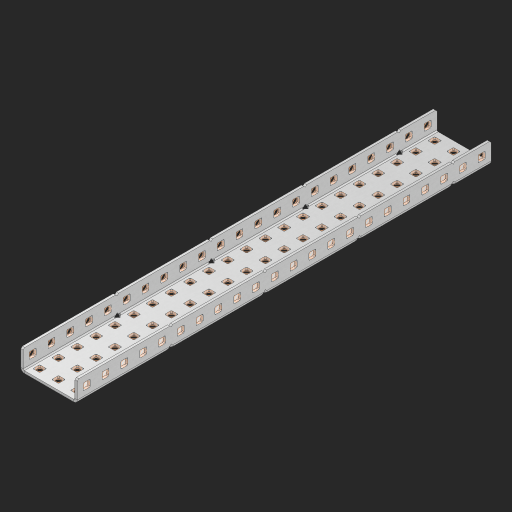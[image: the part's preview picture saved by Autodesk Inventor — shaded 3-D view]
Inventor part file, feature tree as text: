
AUTODESK INVENTOR PART (.ipt)
format: ipt  version: 2023 (Build 270158000, 158)  size: 1,453,568 bytes
history: native  units: in
note: dims shown in document units (in); Inventor stores cm internally (conversion verified against a paired STEP export)
features: other x115, extrude x109, sheet_metal_op x10, sketch x8, mirror x1, pattern_linear x1, chamfer x1
ambient origin geometry x8: Origin, YZ Plane, XZ Plane, XY Plane, X Axis, Y Axis, Z Axis, Center Point
bodies: Solid1 (feature_tree), Body (feature_tree)
feature tree (245):
  other  "Flange Pattern Plane"
  sheet_metal_op  "Flange Pattern"
  sheet_metal_op  "Body Pattern"
  other  "Arc Length"
  mirror  "Notch Mirror"
  pattern_linear  "Notch Pattern"  Spacing1=0.25in  [1 undecoded]
  chamfer  "End Chamfer"
  extrude  "Half Cut"  Depth=0.0625in
  sketch  "Sketch1"  dims[d0=1.5in]
  other  "Plate1"
  sketch  "Sketch2"  dims[d1=11.0in]
  other  "Plate2"
  sheet_metal_op  "Bend1"
  sheet_metal_op  "Corner1"
  sketch  "Sketch3"  dims[d2=0.0625in]
  other  "Flange Pattern Sketch"
  sketch  "Sketch7"  dims[d3=0.0625in]
  other  "Srf1"
  other  "Srf2"
  sketch  "Sketch8"  dims[d4=0.0312in]
  sketch  "Sketch9"  dims[d5=0.125in]
  other  "Srf91"
  sheet_metal_op  "Body Pattern Sketch"
  other  "Srf92"
  sketch  "Sketch13"  dims[d6=0.0625in]
  sketch  "Sketch14"  dims[d7=0.5in d8=90.0deg d9=0.0312in d10=0.25in d11=0.0625in d12=0.0625in d16=0.182in d17=0.02in d18=0.0625in d19=0.0in d20=0.25in d21=0.25in d46=0.172in d47=1.0in d48=0.0in d49=0.182in d50=0.02in d51=0.25in d52=0.25in d53=0.0625in d54=0.0in d55=0.172in d56=1.0in d57=0.0in d60=8.6614in d62=0.5in d63=1.1811in d65=0.5in d85=0.1473in d86=0.1782in d88=0.04in d89=0.0625in d90=0.0in d91=0.04in d92=0.0491in d95=2.5in d96=0.04in d97=0.25in d98=45.0deg d101=0.0in d102=2.497in d131=1.5in d132=8.6614in d134=0.5in d139=0.5in]
  other  "Srf856"
  other  "Srf1310"
  other  "Srf1311"
  other  "Srf1312"
  other  "Srf1376"
  other  "Srf1377"
  other  "Srf1728"
  other  "Srf1755"
  other  "Srf1878"
  other  "Srf1879"
  other  "Srf1880"
  other  "Srf1881"
  other  "Srf1882"
  other  "Srf1883"
  other  "Srf1884"
  other  "Srf1885"
  other  "Srf1886"
  other  "Srf1887"
  other  "Srf1888"
  other  "Srf1889"
  other  "Srf1890"
  other  "Srf1891"
  other  "Srf1892"
  other  "Srf1893"
  other  "Srf1894"
  other  "Srf1895"
  other  "Srf1896"
  other  "Srf1897"
  other  "Srf1898"
  other  "Srf1899"
  other  "Srf1900"
  other  "Srf1901"
  other  "Srf1902"
  other  "Srf1903"
  other  "Srf1904"
  other  "Srf1905"
  other  "Srf1906"
  other  "Srf1907"
  other  "Srf1908"
  other  "Srf1909"
  other  "Srf1910"
  other  "Srf1911"
  other  "Srf1912"
  other  "Srf1913"
  other  "Srf1914"
  other  "Srf1915"
  other  "Srf1942"
  other  "Srf1943"
  other  "Srf1944"
  other  "Srf1945"
  other  "Srf1946"
  other  "Srf1947"
  other  "Srf1948"
  other  "Srf1949"
  other  "Srf1950"
  other  "Srf1951"
  other  "Srf1952"
  other  "Srf1953"
  other  "Srf1954"
  other  "Srf1955"
  other  "Srf1956"
  other  "Srf1957"
  other  "Srf1958"
  other  "Srf1959"
  other  "Srf1960"
  other  "Srf1961"
  other  "Srf1962"
  other  "Srf1963"
  other  "Srf1964"
  other  "Srf1965"
  other  "Srf1966"
  other  "Srf1967"
  other  "Srf1968"
  other  "Srf1969"
  other  "Srf1970"
  other  "Srf1971"
  other  "Srf1972"
  other  "Srf1973"
  other  "Srf1974"
  other  "Srf1975"
  other  "Srf1976"
  other  "Srf1977"
  other  "Srf1978"
  other  "Srf1979"
  other  "Srf1980"
  other  "Srf1981"
  other  "Srf1982"
  other  "Srf1983"
  other  "Srf1984"
  other  "Srf1985"
  other  "Srf1986"
  other  "Srf1987"
  other  "Srf1988"
  other  "Srf1989"
  other  "Srf1990"
  other  "Srf1991"
  other  "Srf1992"
  other  "Srf1993"
  other  "Srf1994"
  other  "Srf1995"
  other  "Srf1996"
  other  "Srf1997"
  other  "Srf1998"
  other  "Srf1999"
  other  "Srf2000"
  other  "Srf2001"
  sheet_metal_op  "Flange Stamp"
  sheet_metal_op  "Flange Circle"
  sheet_metal_op  "Body Stamp"
  sheet_metal_op  "Body Circle"
  sheet_metal_op  "Notch"
  extrude  "ExtrusionSrf2"  Depth=0.0625in
  extrude  "ExtrusionSrf92"  Depth=1.5in
  extrude  "ExtrusionSrf856"  Depth=0.02in
  extrude  "ExtrusionSrf1310"  Depth=0.0625in
  extrude  "ExtrusionSrf1311"  TaperAngle=0.0deg  [1 undecoded]
  extrude  "ExtrusionSrf1312"  Depth=0.25in
  extrude  "ExtrusionSrf1376"  Depth=0.25in
  extrude  "ExtrusionSrf1377"  Depth=1.5in
  extrude  "ExtrusionSrf1728"  Depth=1.5in TaperAngle=0.0deg
  extrude  "ExtrusionSrf1755"  Depth=1.5in
  extrude  "ExtrusionSrf1878"  Depth=0.02in
  extrude  "ExtrusionSrf1879"  Depth=0.25in
  extrude  "ExtrusionSrf1880"  Depth=0.25in
  extrude  "ExtrusionSrf1881"  Depth=0.0625in
  extrude  "ExtrusionSrf1882"  TaperAngle=0.0deg  [1 undecoded]
  extrude  "ExtrusionSrf1883"  Depth=1.5in
  extrude  "ExtrusionSrf1884"  Depth=1.5in TaperAngle=0.0deg
  extrude  "ExtrusionSrf1885"  Depth=1.5in
  extrude  "ExtrusionSrf1886"  Depth=1.5in
  extrude  "ExtrusionSrf1887"  Depth=1.5in
  extrude  "ExtrusionSrf1888"  Depth=1.5in
  extrude  "ExtrusionSrf1889"  Depth=1.5in
  extrude  "ExtrusionSrf1890"  Depth=0.0625in
  extrude  "ExtrusionSrf1891"  TaperAngle=0.0deg  [1 undecoded]
  extrude  "ExtrusionSrf1892"  Depth=1.5in
  extrude  "ExtrusionSrf1893"  Depth=1.5in
  extrude  "ExtrusionSrf1894"  Depth=1.5in
  extrude  "ExtrusionSrf1895"  Depth=0.25in TaperAngle=45.0deg
  extrude  "ExtrusionSrf1896"  TaperAngle=0.0deg  [1 undecoded]
  extrude  "ExtrusionSrf1897"  Depth=1.5in
  extrude  "ExtrusionSrf1898"  Depth=1.5in
  extrude  "ExtrusionSrf1899"  Depth=1.5in
  extrude  "ExtrusionSrf1900"  Depth=1.5in
  extrude  "ExtrusionSrf1901"  Depth=1.5in
  extrude  "ExtrusionSrf1902"  [1 undecoded]
  extrude  "ExtrusionSrf1903"  [1 undecoded]
  extrude  "ExtrusionSrf1904"  [1 undecoded]
  extrude  "ExtrusionSrf1905"  [1 undecoded]
  extrude  "ExtrusionSrf1906"  [1 undecoded]
  extrude  "ExtrusionSrf1907"  [1 undecoded]
  extrude  "ExtrusionSrf1908"  [1 undecoded]
  extrude  "ExtrusionSrf1909"  [1 undecoded]
  extrude  "ExtrusionSrf1910"  [1 undecoded]
  extrude  "ExtrusionSrf1911"  [1 undecoded]
  extrude  "ExtrusionSrf1912"  [1 undecoded]
  extrude  "ExtrusionSrf1913"  [1 undecoded]
  extrude  "ExtrusionSrf1914"  [1 undecoded]
  extrude  "ExtrusionSrf1915"  [1 undecoded]
  extrude  "ExtrusionSrf1942"  [1 undecoded]
  extrude  "ExtrusionSrf1943"  [1 undecoded]
  extrude  "ExtrusionSrf1944"  [1 undecoded]
  extrude  "ExtrusionSrf1945"  [1 undecoded]
  extrude  "ExtrusionSrf1946"  [1 undecoded]
  extrude  "ExtrusionSrf1947"  [1 undecoded]
  extrude  "ExtrusionSrf1948"  [1 undecoded]
  extrude  "ExtrusionSrf1949"  [1 undecoded]
  extrude  "ExtrusionSrf1950"  [1 undecoded]
  extrude  "ExtrusionSrf1951"  [1 undecoded]
  extrude  "ExtrusionSrf1952"  [1 undecoded]
  extrude  "ExtrusionSrf1953"  [1 undecoded]
  extrude  "ExtrusionSrf1954"  [1 undecoded]
  extrude  "ExtrusionSrf1955"  [1 undecoded]
  extrude  "ExtrusionSrf1956"  [1 undecoded]
  extrude  "ExtrusionSrf1957"  [1 undecoded]
  extrude  "ExtrusionSrf1958"  [1 undecoded]
  extrude  "ExtrusionSrf1959"  [1 undecoded]
  extrude  "ExtrusionSrf1960"  [1 undecoded]
  extrude  "ExtrusionSrf1961"  [1 undecoded]
  extrude  "ExtrusionSrf1962"  [1 undecoded]
  extrude  "ExtrusionSrf1963"  [1 undecoded]
  extrude  "ExtrusionSrf1964"  [1 undecoded]
  extrude  "ExtrusionSrf1965"  [1 undecoded]
  extrude  "ExtrusionSrf1966"  [1 undecoded]
  extrude  "ExtrusionSrf1967"  [1 undecoded]
  extrude  "ExtrusionSrf1968"  [1 undecoded]
  extrude  "ExtrusionSrf1969"  [1 undecoded]
  extrude  "ExtrusionSrf1970"  [1 undecoded]
  extrude  "ExtrusionSrf1971"  [1 undecoded]
  extrude  "ExtrusionSrf1972"  [1 undecoded]
  extrude  "ExtrusionSrf1973"  [1 undecoded]
  extrude  "ExtrusionSrf1974"  [1 undecoded]
  extrude  "ExtrusionSrf1975"  [1 undecoded]
  extrude  "ExtrusionSrf1976"  [1 undecoded]
  extrude  "ExtrusionSrf1977"  [1 undecoded]
  extrude  "ExtrusionSrf1978"  [1 undecoded]
  extrude  "ExtrusionSrf1979"  [1 undecoded]
  extrude  "ExtrusionSrf1980"  [1 undecoded]
  extrude  "ExtrusionSrf1981"  [1 undecoded]
  extrude  "ExtrusionSrf1982"  [1 undecoded]
  extrude  "ExtrusionSrf1983"  [1 undecoded]
  extrude  "ExtrusionSrf1984"  [1 undecoded]
  extrude  "ExtrusionSrf1985"  [1 undecoded]
  extrude  "ExtrusionSrf1986"  [1 undecoded]
  extrude  "ExtrusionSrf1987"  [1 undecoded]
  extrude  "ExtrusionSrf1988"  [1 undecoded]
  extrude  "ExtrusionSrf1989"  [1 undecoded]
  extrude  "ExtrusionSrf1990"  [1 undecoded]
  extrude  "ExtrusionSrf1991"  [1 undecoded]
  extrude  "ExtrusionSrf1992"  [1 undecoded]
  extrude  "ExtrusionSrf1993"  [1 undecoded]
  extrude  "ExtrusionSrf1994"  [1 undecoded]
  extrude  "ExtrusionSrf1995"  [1 undecoded]
  extrude  "ExtrusionSrf1996"  [1 undecoded]
  extrude  "ExtrusionSrf1997"  [1 undecoded]
  extrude  "ExtrusionSrf1998"  [1 undecoded]
  extrude  "ExtrusionSrf1999"  [1 undecoded]
  extrude  "ExtrusionSrf2000"  [1 undecoded]
  extrude  "ExtrusionSrf2001"  [1 undecoded]
note: 79 required parameter values undecoded (feature->parameter linkage not recoverable at this tier; creation-order binding heuristic only, values carry confidence <= 0.55)
